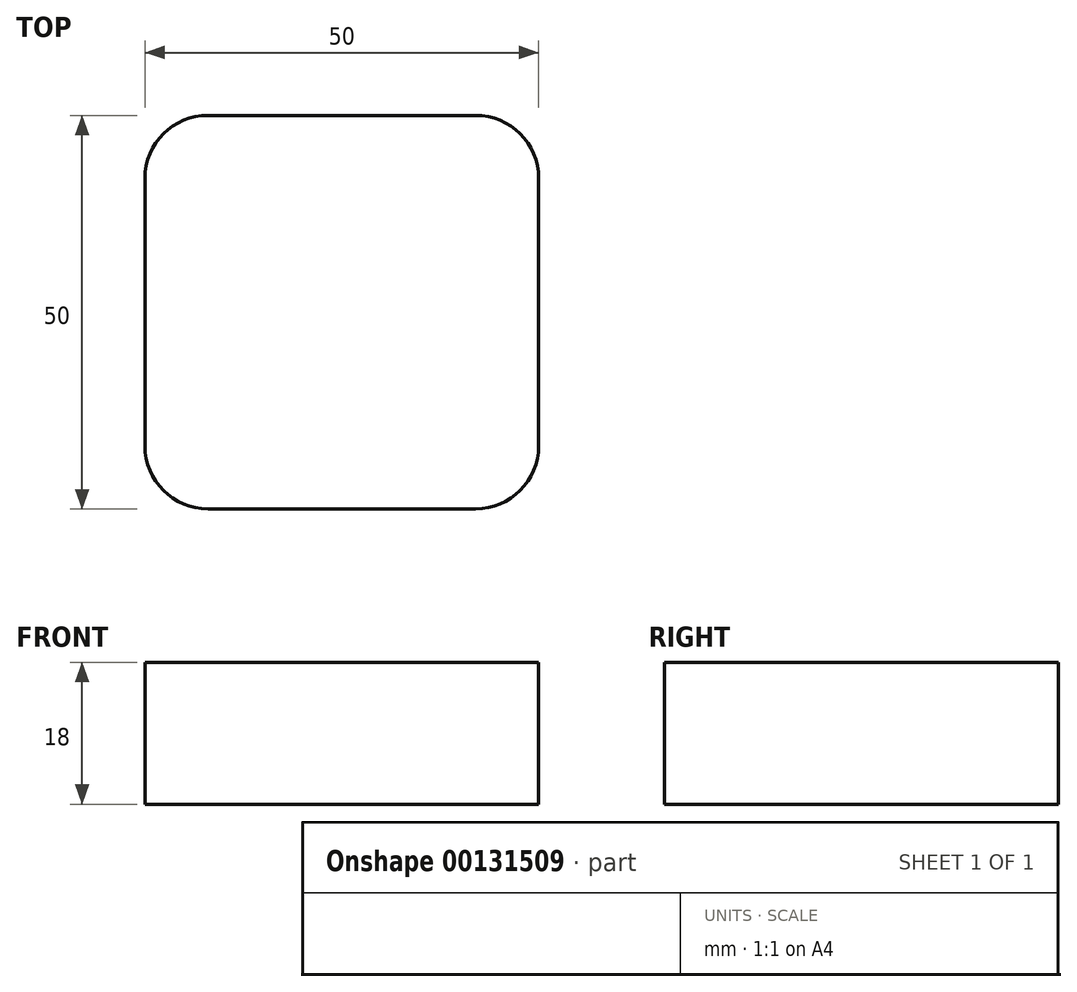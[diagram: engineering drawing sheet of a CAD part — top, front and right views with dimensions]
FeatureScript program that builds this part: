
annotation { "Feature Type Name" : "Feature", "Feature Type Description" : "" }
export const myFeature = defineFeature(function(context is Context, id is Id, definition is map)
    precondition{}
    {
        {
            var Q0;
            Q0=qCreatedBy(makeId("Top.planeOp"),FACE);
            var sketch = newSketch(context, id + "F0", { "sketchPlane" : qUnion([Q0])});
            skLineSegment(sketch, "E0.bottom", {"start": v(25, 25) * mm, "end": v(-25, 25) * mm});
            skLineSegment(sketch, "E0.top", {"start": v(25, -25) * mm, "end": v(-25, -25) * mm});
            skLineSegment(sketch, "E0.left", {"start": v(25, 25) * mm, "end": v(25, -25) * mm});
            skLineSegment(sketch, "E0.right", {"start": v(-25, 25) * mm, "end": v(-25, -25) * mm});
            skPoint(sketch, "E0.middle", {"position": v(0, 0) * mm});
            skSolve(sketch);
        }
        {
            var Q0;
            Q0=qSketchRegion(id+"F0",true);
            extrude(context, id + "F1", {"entities" : qUnion([Q0]), "depth" : 18 * mm});
        }
        {
            var Q0;
            Q0=makeQuery(id+"F1.opExtrude","SWEPT_EDGE",EDGE,{"disambiguationData":[OSD([sQuery(id+"F0.wireOp",EDGE,"E0.top"),sQuery(id+"F0.wireOp",EDGE,"E0.right")])]});
            var Q1;
            Q1=makeQuery(id+"F1.opExtrude","SWEPT_EDGE",EDGE,{"disambiguationData":[OSD([sQuery(id+"F0.wireOp",EDGE,"E0.bottom"),sQuery(id+"F0.wireOp",EDGE,"E0.right")])]});
            var Q2;
            Q2=makeQuery(id+"F1.opExtrude","SWEPT_EDGE",EDGE,{"disambiguationData":[OSD([sQuery(id+"F0.wireOp",EDGE,"E0.top"),sQuery(id+"F0.wireOp",EDGE,"E0.left")])]});
            var Q3;
            Q3=makeQuery(id+"F1.opExtrude","SWEPT_EDGE",EDGE,{"disambiguationData":[OSD([sQuery(id+"F0.wireOp",EDGE,"E0.bottom"),sQuery(id+"F0.wireOp",EDGE,"E0.left")])]});
            fillet(context, id + "F2", {"entities" : qUnion([Q0, Q1, Q2, Q3]), "radius" : 8 * mm, "tangentPropagation" : true, "allowEdgeOverflow" : false});
        }
    });
